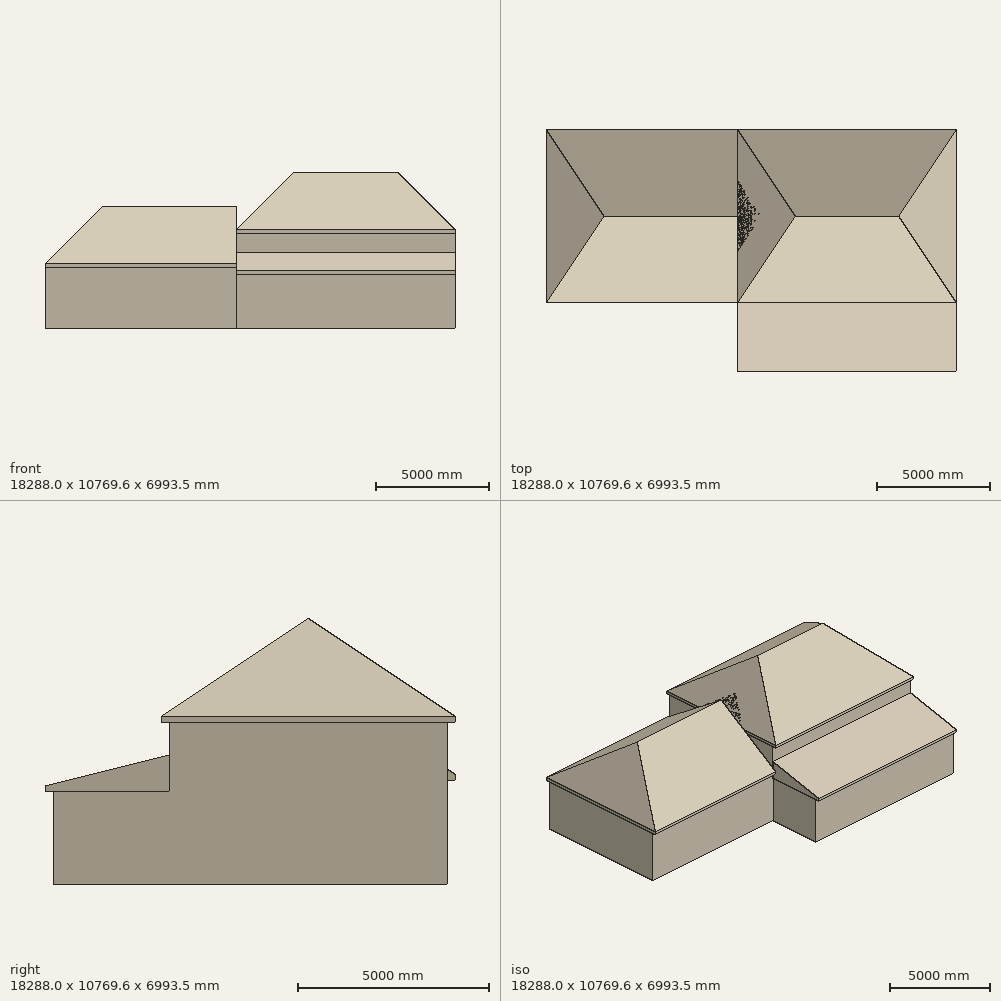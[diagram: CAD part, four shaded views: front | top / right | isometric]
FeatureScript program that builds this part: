
annotation { "Feature Type Name" : "Feature", "Feature Type Description" : "" }
export const myFeature = defineFeature(function(context is Context, id is Id, definition is map)
    precondition{}
    {
        {
            var Q0;
            Q0=qCreatedBy(makeId("Top.planeOp"),FACE);
            var sketch = newSketch(context, id + "F0", { "sketchPlane" : qUnion([Q0])});
            skLineSegment(sketch, "E0.bottom", {"start": v(0, 0) * mm, "end": v(9753.6, 0) * mm});
            skLineSegment(sketch, "E0.top", {"start": v(0, -7315.2) * mm, "end": v(9753.6, -7315.2) * mm});
            skLineSegment(sketch, "E0.left", {"start": v(0, 0) * mm, "end": v(0, -7315.2) * mm});
            skLineSegment(sketch, "E0.right", {"start": v(9753.6, 0) * mm, "end": v(9753.6, -7315.2) * mm});
            skSolve(sketch);
        }
        {
            var Q0;
            Q0=makeQuery(id+"F0.imprint","IMPRINT",FACE,{"disambiguationData":[TD([[makeQuery(id+"F0.imprint","IMPRINT",EDGE,{"derivedFrom":sQuery(id+"F0.wireOp",EDGE,"E0.bottom")}),-1.0]])]});
            extrude(context, id + "F1", {"entities" : qUnion([Q0]), "depth" : 4267.2 * mm});
        }
        {
            var Q0;
            Q0=makeQuery(id+"F1.opExtrude","SWEPT_FACE",FACE,{"disambiguationData":[OSD([sQuery(id+"F0.wireOp",EDGE,"E0.right")])]});
            var sketch = newSketch(context, id + "F2", { "sketchPlane" : qUnion([Q0])});
            skLineSegment(sketch, "E1", {"start": v(-7518.4, 4267.2) * mm, "end": v(203.2, 4267.2) * mm});
            skLineSegment(sketch, "E2", {"start": v(203.2, 4267.2) * mm, "end": v(203.2, 4419.6) * mm});
            skLineSegment(sketch, "E3", {"start": v(203.2, 4419.6) * mm, "end": v(-3657.6, 6993.46) * mm});
            skLineSegment(sketch, "E4", {"start": v(-3657.6, 6993.46) * mm, "end": v(-7518.4, 4419.6) * mm});
            skLineSegment(sketch, "E5", {"start": v(-7518.4, 4419.6) * mm, "end": v(-7518.4, 4267.2) * mm});
            skSolve(sketch);
        }
        {
            var Q0;
            {var subQ0=sQuery(id+"F2.wireOp",EDGE,"E2");Q0=makeQuery(id+"F2.imprint","IMPRINT",FACE,{"disambiguationData":[TD([[makeQuery(id+"F2.imprint","IMPRINT",EDGE,{"derivedFrom":subQ0}),1.0]])]});}
            extrude(context, id + "F3", {"entities" : qUnion([Q0]), "oppositeDirection" : true, "depth" : 9753.6 * mm});
        }
        {
            var Q0;
            Q0=qCreatedBy(makeId("Top.planeOp"),FACE);
            var sketch = newSketch(context, id + "F4", { "sketchPlane" : qUnion([Q0])});
            skLineSegment(sketch, "E6.bottom", {"start": v(0, -7315.2) * mm, "end": v(9753.6, -7315.2) * mm});
            skLineSegment(sketch, "E6.top", {"start": v(0, -10363.2) * mm, "end": v(9753.6, -10363.2) * mm});
            skLineSegment(sketch, "E6.left", {"start": v(0, -7315.2) * mm, "end": v(0, -10363.2) * mm});
            skLineSegment(sketch, "E6.right", {"start": v(9753.6, -7315.2) * mm, "end": v(9753.6, -10363.2) * mm});
            skSolve(sketch);
        }
        {
            var Q0;
            Q0=makeQuery(id+"F4.imprint","IMPRINT",FACE,{"disambiguationData":[TD([[makeQuery(id+"F4.imprint","IMPRINT",EDGE,{"derivedFrom":sQuery(id+"F4.wireOp",EDGE,"E6.bottom")}),-1.0]])]});
            extrude(context, id + "F5", {"entities" : qUnion([Q0]), "operationType" : NewBodyOperationType.ADD, "depth" : 2438.4 * mm});
        }
        {
            var Q0;
            Q0=makeQuery(id+"F5.boolean.opBoolean","MERGE",FACE,{"derivedFrom":[makeQuery(id+"F1.opExtrude","SWEPT_FACE",FACE,{"disambiguationData":[OSD([sQuery(id+"F0.wireOp",EDGE,"E0.right")])]}),makeQuery(id+"F5.opExtrude","SWEPT_FACE",FACE,{"disambiguationData":[OSD([sQuery(id+"F4.wireOp",EDGE,"E6.right")])]})]});
            var sketch = newSketch(context, id + "F6", { "sketchPlane" : qUnion([Q0])});
            skLineSegment(sketch, "E7", {"start": v(-10566.4, 2438.4) * mm, "end": v(-10566.4, 2590.8) * mm});
            skLineSegment(sketch, "E8", {"start": v(-10566.4, 2590.8) * mm, "end": v(-7315.2, 3403.83) * mm});
            skLineSegment(sketch, "E9", {"start": v(-7315.2, 3403.83) * mm, "end": v(-7315.2, 2438.4) * mm});
            skLineSegment(sketch, "E10", {"start": v(-7315.2, 2438.4) * mm, "end": v(-10566.4, 2438.4) * mm});
            skSolve(sketch);
        }
        {
            var Q0;
            {var subQ3=sQuery(id+"F6.wireOp",EDGE,"edNapGtM-GmXn-vVtZ-yoxO-ZXmBFordLB6F");Q0=makeQuery(id+"F6.imprint","IMPRINT",FACE,{"disambiguationData":[TD([[makeQuery(id+"F6.imprint","IMPRINT",EDGE,{"derivedFrom":subQ3}),-1.0]])]});}
            var Q1;
            {var subQ3=sQuery(id+"F6.wireOp",EDGE,"E7");Q1=makeQuery(id+"F6.imprint","IMPRINT",FACE,{"disambiguationData":[TD([[makeQuery(id+"F6.imprint","IMPRINT",EDGE,{"derivedFrom":subQ3}),-1.0]])]});}
            var Q2;
            Q2=makeQuery(id+"F5.boolean.opBoolean","MERGE",FACE,{"derivedFrom":[makeQuery(id+"F1.opExtrude","SWEPT_FACE",FACE,{"disambiguationData":[OSD([sQuery(id+"F0.wireOp",EDGE,"E0.left")])]}),makeQuery(id+"F5.opExtrude","SWEPT_FACE",FACE,{"disambiguationData":[OSD([sQuery(id+"F4.wireOp",EDGE,"E6.left")])]})]});
            extrude(context, id + "F7", {"entities" : qUnion([Q0, Q1]), "endBound" : BoundingType.UP_TO_SURFACE, "oppositeDirection" : true, "endBoundEntityFace" : qUnion([Q2]), "depth" : 6705.6 * mm});
        }
        {
            var Q0;
            Q0=qCreatedBy(makeId("Top.planeOp"),FACE);
            var sketch = newSketch(context, id + "F8", { "sketchPlane" : qUnion([Q0])});
            skLineSegment(sketch, "E11.bottom", {"start": v(0, 0) * mm, "end": v(-8534.4, 0) * mm});
            skLineSegment(sketch, "E11.top", {"start": v(0, -7315.2) * mm, "end": v(-8534.4, -7315.2) * mm});
            skLineSegment(sketch, "E11.left", {"start": v(0, 0) * mm, "end": v(0, -7315.2) * mm});
            skLineSegment(sketch, "E11.right", {"start": v(-8534.4, 0) * mm, "end": v(-8534.4, -7315.2) * mm});
            skSolve(sketch);
        }
        {
            var Q0;
            Q0=makeQuery(id+"F8.imprint","IMPRINT",FACE,{"disambiguationData":[TD([[makeQuery(id+"F8.imprint","IMPRINT",EDGE,{"derivedFrom":sQuery(id+"F8.wireOp",EDGE,"E11.bottom")}),1.0]])]});
            extrude(context, id + "F9", {"entities" : qUnion([Q0]), "depth" : 2743.2 * mm});
        }
        {
            var Q0;
            Q0=makeQuery(id+"F9.opExtrude","SWEPT_FACE",FACE,{"disambiguationData":[OSD([sQuery(id+"F8.wireOp",EDGE,"E11.right")])]});
            var sketch = newSketch(context, id + "F10", { "sketchPlane" : qUnion([Q0])});
            skLineSegment(sketch, "E12", {"start": v(3657.6, 5469.46) * mm, "end": v(-203.2, 2895.6) * mm});
            skLineSegment(sketch, "E13", {"start": v(-203.2, 2895.6) * mm, "end": v(-203.2, 2743.2) * mm});
            skLineSegment(sketch, "E14", {"start": v(-203.2, 2743.2) * mm, "end": v(7518.4, 2743.2) * mm});
            skLineSegment(sketch, "E15", {"start": v(7518.4, 2743.2) * mm, "end": v(7518.4, 2895.6) * mm});
            skLineSegment(sketch, "E16", {"start": v(7518.4, 2895.6) * mm, "end": v(3657.6, 5469.46) * mm});
            skSolve(sketch);
        }
        {
            var Q0;
            Q0=makeQuery(id+"F10.imprint","IMPRINT",FACE,{"disambiguationData":[TD([[makeQuery(id+"F10.imprint","IMPRINT",EDGE,{"derivedFrom":sQuery(id+"F10.wireOp",EDGE,"E12")}),1.0]])]});
            extrude(context, id + "F11", {"entities" : qUnion([Q0]), "oppositeDirection" : true, "depth" : 10972.8 * mm});
        }
        {
            var Q0;
            Q0=makeQuery(id+"F11.opExtrude","SWEPT_FACE",FACE,{"disambiguationData":[OSD([sQuery(id+"F10.wireOp",EDGE,"E15")])]});
            var sketch = newSketch(context, id + "F12", { "sketchPlane" : qUnion([Q0])});
            skLineSegment(sketch, "E17", {"start": v(-8534.4, 5469.46) * mm, "end": v(-8534.4, 2895.6) * mm});
            skLineSegment(sketch, "E18", {"start": v(-8534.4, 2895.6) * mm, "end": v(-5960.54, 5469.46) * mm});
            skLineSegment(sketch, "E19", {"start": v(-5960.54, 5469.46) * mm, "end": v(-8534.4, 5469.46) * mm});
            skSolve(sketch);
        }
        {
            var Q0;
            Q0=makeQuery(id+"F12.imprint","IMPRINT",FACE,{"disambiguationData":[TD([[makeQuery(id+"F12.imprint","IMPRINT",EDGE,{"derivedFrom":sQuery(id+"F12.wireOp",EDGE,"E17")}),1.0]])]});
            extrude(context, id + "F13", {"entities" : qUnion([Q0]), "operationType" : NewBodyOperationType.REMOVE, "endBound" : BoundingType.THROUGH_ALL, "oppositeDirection" : true, "depth" : 25.4 * mm});
        }
        {
            var Q0;
            Q0=makeQuery(id+"F3.opExtrude","SWEPT_FACE",FACE,{"disambiguationData":[OSD([sQuery(id+"F2.wireOp",EDGE,"E5")])]});
            var sketch = newSketch(context, id + "F14", { "sketchPlane" : qUnion([Q0])});
            skLineSegment(sketch, "E20", {"start": v(2573.86, 6993.46) * mm, "end": v(0, 6993.46) * mm});
            skLineSegment(sketch, "E21", {"start": v(0, 6993.46) * mm, "end": v(0, 4419.6) * mm});
            skLineSegment(sketch, "E22", {"start": v(0, 4419.6) * mm, "end": v(2573.86, 6993.46) * mm});
            skLineSegment(sketch, "E23", {"start": v(7179.74, 6993.46) * mm, "end": v(9753.6, 6993.46) * mm});
            skLineSegment(sketch, "E24", {"start": v(9753.6, 6993.46) * mm, "end": v(9753.6, 4419.6) * mm});
            skLineSegment(sketch, "E25", {"start": v(9753.6, 4419.6) * mm, "end": v(7179.74, 6993.46) * mm});
            skSolve(sketch);
        }
        {
            var Q0;
            Q0=makeQuery(id+"F14.imprint","IMPRINT",FACE,{"disambiguationData":[TD([[makeQuery(id+"F14.imprint","IMPRINT",EDGE,{"derivedFrom":sQuery(id+"F14.wireOp",EDGE,"E20")}),1.0]])]});
            var Q1;
            Q1=makeQuery(id+"F14.imprint","IMPRINT",FACE,{"disambiguationData":[TD([[makeQuery(id+"F14.imprint","IMPRINT",EDGE,{"derivedFrom":sQuery(id+"F14.wireOp",EDGE,"E23")}),-1.0]])]});
            extrude(context, id + "F15", {"entities" : qUnion([Q0, Q1]), "operationType" : NewBodyOperationType.REMOVE, "endBound" : BoundingType.THROUGH_ALL, "oppositeDirection" : true, "depth" : 25.4 * mm});
        }
    });
